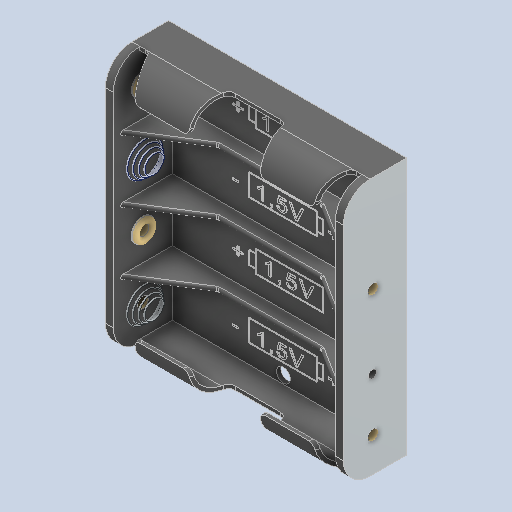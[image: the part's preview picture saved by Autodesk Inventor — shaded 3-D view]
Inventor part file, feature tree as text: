
AUTODESK INVENTOR PART (.ipt)
format: ipt  version: 2024 (Build 280153000, 153)  size: 1,385,984 bytes
history: native  units: in
note: dims shown in document units (in); Inventor stores cm internally (conversion verified against a paired STEP export)
features: other x6, sweep x1
ambient origin geometry x8: Origin, YZ Plane, XZ Plane, XY Plane, X Axis, Y Axis, Z Axis, Center Point
bodies: Solid1 (feature_tree), Solid2 (feature_tree), Solid3 (feature_tree), Solid4 (feature_tree), Solid5 (feature_tree)
feature tree (7):
  other  "Plane4"
  other  "Piano2"
  other  "Taglio-Estrusione2"
  sweep  "Sweep2"
  other  "Corpo-Sposta_copia4"
  other  "Corpo-Sposta_copia5[1]"
  other  "Corpo-Sposta_copia5[2]"
